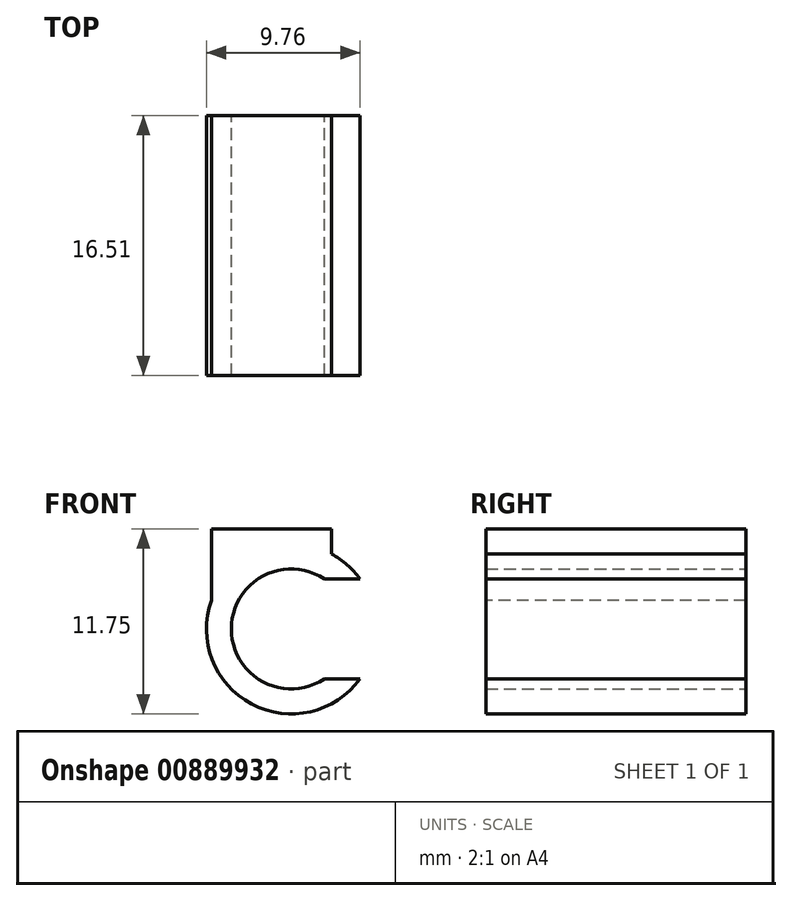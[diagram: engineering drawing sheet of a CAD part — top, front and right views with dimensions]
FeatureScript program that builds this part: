
annotation { "Feature Type Name" : "Feature", "Feature Type Description" : "" }
export const myFeature = defineFeature(function(context is Context, id is Id, definition is map)
    precondition{}
    {
        {
            var Q0;
            Q0=qCreatedBy(makeId("Front.planeOp"),FACE);
            var sketch = newSketch(context, id + "F0", { "sketchPlane" : qUnion([Q0])});
            skArc(sketch, "E0", {"start": v(2.1, 3.18) * mm, "mid": v(-3.81, 0) * mm, "end": v(2.1, -3.18) * mm});
            skArc(sketch, "E1.0", {"start": v(4.36, 3.18) * mm, "mid": v(-5.4, 0) * mm, "end": v(4.36, -3.18) * mm});
            skLineSegment(sketch, "E2", {"start": v(-5.4, 0) * mm, "end": v(5.4, 0) * mm, "construction": true});
            skLineSegment(sketch, "E3", {"start": v(-6.63, 3.18) * mm, "end": v(7.37, 3.18) * mm, "construction": true});
            skLineSegment(sketch, "E4", {"start": v(-6.34, -3.18) * mm, "end": v(7.33, -3.18) * mm, "construction": true});
            skLineSegment(sketch, "E5", {"start": v(2.1, 3.18) * mm, "end": v(4.36, 3.18) * mm});
            skLineSegment(sketch, "E6", {"start": v(2.1, -3.18) * mm, "end": v(4.36, -3.18) * mm});
            skPoint(sketch, "E6.startSnap0", {"position": v(0.5, -3.18) * mm});
            skSolve(sketch);
        }
        {
            var Q0;
            Q0=qSketchRegion(id+"F0",true);
            extrude(context, id + "F1", {"entities" : qUnion([Q0]), "depth" : 73.66 * mm, "offsetDistance" : 25.4 * mm});
        }
        {
            var Q0;
            Q0=makeQuery(id+"F1.opExtrude","CAP_FACE",FACE,{"disambiguationData":[OSD([sQuery(id+"F0.wireOp",EDGE,"E0"),sQuery(id+"F0.wireOp",EDGE,"E1.0"),sQuery(id+"F0.wireOp",EDGE,"E5"),sQuery(id+"F0.wireOp",EDGE,"E6")])],"isStart":false});
            var sketch = newSketch(context, id + "F2", { "sketchPlane" : qUnion([Q0])});
            skLineSegment(sketch, "E7", {"start": v(-5.08, 1.82) * mm, "end": v(-5.08, 6.35) * mm});
            skLineSegment(sketch, "E8", {"start": v(2.54, 4.76) * mm, "end": v(2.54, 6.35) * mm});
            skLineSegment(sketch, "E9", {"start": v(2.54, 6.35) * mm, "end": v(-5.08, 6.35) * mm});
            skArc(sketch, "E10.0", {"start": v(2.54, 4.76) * mm, "mid": v(-1.94, 5.04) * mm, "end": v(-5.08, 1.82) * mm});
            skPoint(sketch, "E11.orphan", {"position": v(4.36, -3.18) * mm});
            skPoint(sketch, "E12.orphan", {"position": v(4.36, 3.18) * mm});
            skSolve(sketch);
        }
        {
            var Q0;
            Q0=qSketchRegion(id+"F2",true);
            var Q1;
            Q1=makeQuery(id+"F1.opExtrude","CAP_FACE",FACE,{"disambiguationData":[OSD([sQuery(id+"F0.wireOp",EDGE,"E0"),sQuery(id+"F0.wireOp",EDGE,"E1.0"),sQuery(id+"F0.wireOp",EDGE,"E5"),sQuery(id+"F0.wireOp",EDGE,"E6")])],"isStart":true});
            extrude(context, id + "F3", {"entities" : qUnion([Q0]), "operationType" : NewBodyOperationType.ADD, "endBound" : BoundingType.UP_TO_SURFACE, "oppositeDirection" : true, "depth" : 25.4 * mm, "endBoundEntityFace" : qUnion([Q1]), "offsetDistance" : 25.4 * mm});
        }
        {
            var Q0;
            Q0=makeQuery(id+"F3.opExtrude","SWEPT_FACE",FACE,{"disambiguationData":[OSD([sQuery(id+"F2.wireOp",EDGE,"E9")])]});
            var sketch = newSketch(context, id + "F4", { "sketchPlane" : qUnion([Q0])});
            skLineSegment(sketch, "E13", {"start": v(-5.08, -36.83) * mm, "end": v(2.54, -36.83) * mm, "construction": true});
            skLineSegment(sketch, "E14", {"start": v(-13.97, -68.58) * mm, "end": v(11.43, -68.58) * mm});
            skLineSegment(sketch, "E15", {"start": v(-1.27, -73.66) * mm, "end": v(-1.27, 0) * mm, "construction": true});
            skLineSegment(sketch, "E16", {"start": v(-13.97, -68.58) * mm, "end": v(-13.97, -5.08) * mm, "construction": true});
            skLineSegment(sketch, "E17", {"start": v(-13.97, -5.08) * mm, "end": v(11.43, -5.08) * mm});
            skLineSegment(sketch, "E18", {"start": v(11.43, -5.08) * mm, "end": v(11.43, -68.58) * mm, "construction": true});
            skLineSegment(sketch, "E19.0", {"start": v(-13.97, -11.43) * mm, "end": v(11.43, -11.43) * mm});
            skLineSegment(sketch, "E20", {"start": v(-13.97, -5.08) * mm, "end": v(-13.97, -11.43) * mm});
            skLineSegment(sketch, "E21", {"start": v(11.43, -5.08) * mm, "end": v(11.43, -11.43) * mm});
            skLineSegment(sketch, "E22.0", {"start": v(-13.97, -62.23) * mm, "end": v(11.43, -62.23) * mm});
            skLineSegment(sketch, "E23", {"start": v(11.43, -62.23) * mm, "end": v(11.43, -68.58) * mm});
            skLineSegment(sketch, "E24", {"start": v(-13.97, -62.23) * mm, "end": v(-13.97, -68.58) * mm});
            skSolve(sketch);
        }
        {
            var Q0;
            Q0=qSketchRegion(id+"F4",true);
            extrude(context, id + "F5", {"entities" : qUnion([Q0]), "operationType" : NewBodyOperationType.ADD, "depth" : 69.85 * mm, "offsetDistance" : 25.4 * mm});
        }
        {
            var Q0;
            Q0=makeQuery(id+"F5.opExtrude","SWEPT_FACE",FACE,{"disambiguationData":[OSD([sQuery(id+"F4.wireOp",EDGE,"E14")])]});
            var sketch = newSketch(context, id + "F6", { "sketchPlane" : qUnion([Q0])});
            skLineSegment(sketch, "E25", {"start": v(-1.27, 76.2) * mm, "end": v(-1.27, -11.05) * mm, "construction": true});
            skLineSegment(sketch, "E26.0", {"start": v(-7.62, 76.2) * mm, "end": v(-7.62, 12.7) * mm});
            skLineSegment(sketch, "E27.0", {"start": v(5.08, 76.2) * mm, "end": v(5.08, 12.7) * mm});
            skLineSegment(sketch, "E28", {"start": v(-7.62, 12.7) * mm, "end": v(5.08, 12.7) * mm});
            skLineSegment(sketch, "E29", {"start": v(-7.62, 76.2) * mm, "end": v(5.08, 76.2) * mm});
            skSolve(sketch);
        }
        {
            var Q0;
            Q0=qSketchRegion(id+"F6",true);
            var Q1;
            Q1=makeQuery(id+"F5.opExtrude","SWEPT_FACE",FACE,{"disambiguationData":[OSD([sQuery(id+"F4.wireOp",EDGE,"E17")])]});
            extrude(context, id + "F7", {"entities" : qUnion([Q0]), "operationType" : NewBodyOperationType.REMOVE, "endBound" : BoundingType.UP_TO_SURFACE, "oppositeDirection" : true, "depth" : 25.4 * mm, "endBoundEntityFace" : qUnion([Q1]), "offsetDistance" : 25.4 * mm});
        }
        {
            var Q0;
            Q0=makeQuery(id+"F3.boolean.opBoolean","MERGE",FACE,{"derivedFrom":[makeQuery(id+"F1.opExtrude","CAP_FACE",FACE,{"disambiguationData":[OSD([sQuery(id+"F0.wireOp",EDGE,"E0"),sQuery(id+"F0.wireOp",EDGE,"E1.0"),sQuery(id+"F0.wireOp",EDGE,"E5"),sQuery(id+"F0.wireOp",EDGE,"E6")])],"isStart":true}),makeQuery(id+"F3.opExtrude","CAP_FACE",FACE,{"disambiguationData":[OSD([sQuery(id+"F2.wireOp",EDGE,"E7"),sQuery(id+"F2.wireOp",EDGE,"E8"),sQuery(id+"F2.wireOp",EDGE,"E9"),sQuery(id+"F2.wireOp",EDGE,"E10.0")])],"isStart":false})]});
            var sketch = newSketch(context, id + "F8", { "sketchPlane" : qUnion([Q0])});
            skLineSegment(sketch, "E30.0", {"start": v(-11.43, 76.2) * mm, "end": v(-11.43, 6.35) * mm, "construction": true});
            skLineSegment(sketch, "E31", {"start": v(-11.43, 76.2) * mm, "end": v(-11.43, -6.35) * mm});
            skLineSegment(sketch, "E32", {"start": v(-11.43, -6.35) * mm, "end": v(13.97, -6.35) * mm});
            skLineSegment(sketch, "E33", {"start": v(13.97, 76.2) * mm, "end": v(13.97, -6.35) * mm});
            skLineSegment(sketch, "E34", {"start": v(-11.43, 76.2) * mm, "end": v(13.97, 76.2) * mm});
            skSolve(sketch);
        }
        {
            var Q0;
            Q0=qSketchRegion(id+"F8",true);
            extrude(context, id + "F9", {"entities" : qUnion([Q0]), "operationType" : NewBodyOperationType.REMOVE, "oppositeDirection" : true, "depth" : 57.15 * mm, "offsetDistance" : 25.4 * mm});
        }
        {
            var Q0;
            {var subQ0=sQuery(id+"F4.wireOp",EDGE,"E22.0");var subQ1=sQuery(id+"F4.wireOp",EDGE,"E14");var subQ2=sQuery(id+"F4.wireOp",EDGE,"E24");Q0=makeQuery(id+"F5.boolean.opBoolean","SPLIT",FACE,{"disambiguationData":[TD([makeQuery(id+"F3.opExtrude","SWEPT_FACE",FACE,{"disambiguationData":[OSD([sQuery(id+"F2.wireOp",EDGE,"E7")])]})])],"derivedFrom":makeQuery(id+"F5.opExtrude","CAP_FACE",FACE,{"disambiguationData":[OSD([subQ1,subQ0,sQuery(id+"F4.wireOp",EDGE,"E23"),subQ2])],"isStart":true})});}
            var sketch = newSketch(context, id + "F10", { "sketchPlane" : qUnion([Q0])});
            skLineSegment(sketch, "E35.0", {"start": v(-13.97, 62.23) * mm, "end": v(-13.97, 68.58) * mm});
            skLineSegment(sketch, "E36.0", {"start": v(11.43, 62.23) * mm, "end": v(11.43, 68.58) * mm});
            skLineSegment(sketch, "E37", {"start": v(-13.97, 68.58) * mm, "end": v(11.43, 68.58) * mm});
            skLineSegment(sketch, "E38", {"start": v(-13.97, 62.23) * mm, "end": v(11.43, 62.23) * mm});
            skSolve(sketch);
        }
        {
            var Q0;
            Q0 = qSketchRegion(id + "F10", true);
            extrude(context, id + "F11", {"entities" : qUnion([Q0]), "operationType" : NewBodyOperationType.REMOVE, "endBound" : BoundingType.THROUGH_ALL, "oppositeDirection" : true, "depth" : 25.4 * mm, "offsetDistance" : 25.4 * mm});
        }
    });
